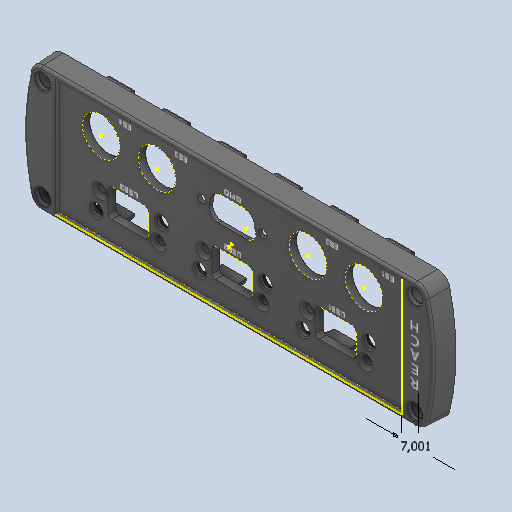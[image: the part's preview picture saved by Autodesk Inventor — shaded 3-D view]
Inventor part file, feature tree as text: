
AUTODESK INVENTOR PART (.ipt)
format: ipt  version: 2024.2 (Build 282272000, 272)  size: 1,141,248 bytes
history: native  units: mm
features: extrude x9, chamfer x4, fillet x3, sketch x3, plane x2, mirror x1, hole x1, projected_geometry x1, other x1
ambient origin geometry x8: Origin, YZ Plane, XZ Plane, XY Plane, X Axis, Y Axis, Z Axis, Center Point
bodies: Solid1 (feature_tree)
feature tree (25):
  extrude  "Extrusion1"  TaperAngle=0.0deg  [1 undecoded]
  fillet  "Fillet1"  Radius=6.9mm
  plane  "Work Plane1"
  extrude  "Extrusion4"  [1 undecoded]
  chamfer  "Chamfer2"  Distance=11.5mm
  mirror  "Mirror1"
  plane  "Work Plane2"
  extrude  "Extrusion6"  Depth=1.0mm
  extrude  "Extrusion7"  Depth=1.0mm
  chamfer  "Chamfer3"  [1 undecoded]
  extrude  "Extrusion9"  Depth=1.0mm
  fillet  "Fillet3"  [1 undecoded]
  hole  "Hole1"  [1 undecoded]
  extrude  "Extrusion10"  Depth=1.0mm
  extrude  "Extrusion11"  Depth=1.0mm
  extrude  "Extrusion12"  Depth=1.0mm
  fillet  "Fillet4"  Radius=12.495mm
  chamfer  "Chamfer4"  Distance=5.23mm
  chamfer  "Chamfer5"  Distance=4.77mm
  extrude  "Extrusion13"  TaperAngle=0.0deg  [1 undecoded]
  sketch  "Sketch20"  dims[d23=1.35mm d26=-1.5mm]
  sketch  "Sketch21"  dims[d40=15.4mm d41=11.5mm d42=54.0mm d43=15.4mm d44=0.0mm d45=31.0mm d46=0.0mm d47=0.0mm d48=0.2mm d49=2.0mm d50=45.0deg d53=1.745329mm d54=10.46mm d56=3.3mm d57=12.495mm d58=5.23mm d59=4.77mm d60=0.0mm d61=0.0mm d63=3.72mm d64=9.51mm d65=4.85mm d66=4.85mm d67=27.0mm d68=9.0mm d69=3.3mm d70=3.3mm d71=24.0mm d72=16.55mm d73=11.55mm d74=6.35mm d75=1.85mm d76=5.225mm d77=6.9mm d78=10.075mm d79=10.075mm d80=42.584mm d82=7.0mm d83=10.0mm d84=0.0mm d85=0.5mm d86=2.0mm d87=45.0deg d101=10.075mm d102=4.85mm d103=4.85mm d104=27.0mm d105=9.0mm d106=3.3mm d107=3.3mm d108=24.0mm d109=16.55mm d110=11.55mm d111=6.35mm d112=1.85mm d113=5.225mm d114=10.075mm d115=12.0mm d116=6.9mm d117=42.584mm d118=7.0mm d119=7.0mm d122=12.0mm d123=41.0mm d124=2.0mm d125=0.0mm d126=2.0mm d127=3.25mm d128=6.0mm d129=6.25mm d130=2.0mm d131=90.0deg d132=8.0mm d133=20.594885mm d134=10.0mm d135=0.0mm d136=10.0mm d137=0.0mm d138=0.2mm d139=0.0mm d140=3.0mm d141=0.2mm d142=2.0mm d143=45.0deg d144=0.2mm d145=2.0mm d146=45.0deg d147=10.0mm d148=0.0mm d149=8.0mm d150=12.5mm d151=8.0mm d152=12.5mm d153=12.5mm d154=8.0mm d155=8.0mm d156=12.5mm d157=4.5mm d160=4.5mm d161=1.0mm d164=1.0mm d165=1.0mm d166=2.25mm d167=28.699852mm d169=20.0mm d171=42.584mm d172=10.0mm d174=10.0mm d176=7.0mm d177=7.0mm d178=7.0mm d179=1.0mm d180=4.5mm d181=7.001437mm]
  sketch  "Sketch14"  dims[d3=9.0mm d15=0.0mm d16=0.0mm d21=6.9mm]
  projected_geometry  "Projected Loop5"
  other  "1009799_3D"
note: 6 required parameter values undecoded (feature->parameter linkage not recoverable at this tier; creation-order binding heuristic only, values carry confidence <= 0.55)
